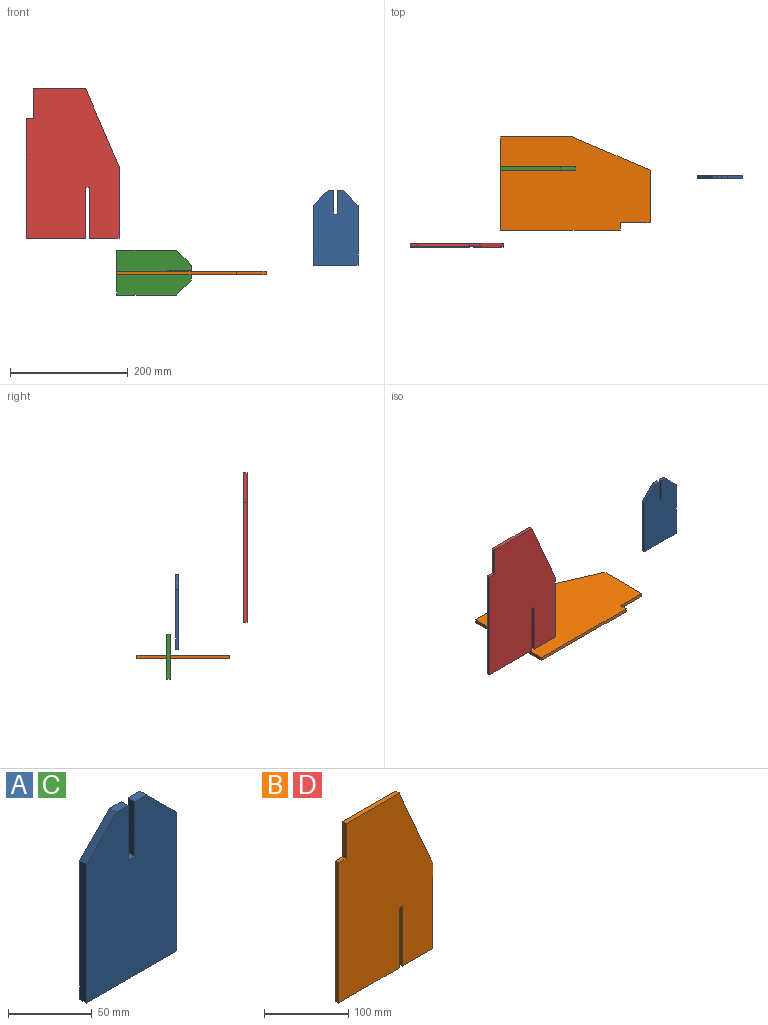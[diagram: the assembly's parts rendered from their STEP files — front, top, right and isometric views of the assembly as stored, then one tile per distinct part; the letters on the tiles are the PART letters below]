
ASSEMBLY  parts=4 mates=1
PART A: 12 faces, bbox 76.2x5.8x127 mm
  f0: plane 9.82x5.77mm, normal (0,0,1), area 56.6mm2, adj f1,f9,f10,f11
  f1: plane 25.4x25.4mm, normal (-0.71,0,0.71), area 207.1mm2, adj f0,f2,f10,f11
  f2: plane 101.6x5.77mm, normal (-1,0,0), area 585.8mm2, adj f1,f3,f10,f11
  f3: plane 76.2x5.77mm, normal (0,0,-1), area 439.4mm2, adj f2,f4,f10,f11
  f4: plane 101.6x5.77mm, normal (1,0,0), area 585.8mm2, adj f3,f5,f10,f11
  f5: plane 25.4x25.4mm, normal (0.71,0,0.71), area 207.1mm2, adj f4,f6,f10,f11
  f6: plane 9.82x5.77mm, normal (0,0,1), area 56.6mm2, adj f5,f7,f10,f11
  f7: plane 40.13x5.77mm, normal (-1,0,0), area 231.4mm2, adj f6,f8,f10,f11
  f8: plane 5.77x5.77mm, normal (0,0,1), area 33.2mm2, adj f7,f9,f10,f11
  f9: plane 40.13x5.77mm, normal (1,0,0), area 231.4mm2, adj f0,f8,f10,f11
  f10: plane 127x76.2mm, normal (0,-1,0), area 8800.8mm2, adj f0,f1,f2,f3,f4,f5,f6,f7
  f11: plane 127x76.2mm, normal (0,1,0), area 8800.8mm2, adj f0,f1,f2,f3,f4,f5,f6,f7
PART B: 13 faces, bbox 158.2x5.8x254 mm
  f0: plane 86.87x5.77mm, normal (1,0,0), area 500.9mm2, adj f1,f10,f11,f12
  f1: plane 5.77x5.77mm, normal (0,0,-1), area 33.2mm2, adj f0,f2,f11,f12
  f2: plane 86.86x5.77mm, normal (-1,0,0), area 500.8mm2, adj f1,f3,f11,f12
  f3: plane 50.8x5.77mm, normal (0,0,-1), area 292.9mm2, adj f2,f4,f11,f12
  f4: plane 122.77x5.77mm, normal (1,0,0), area 707.8mm2, adj f3,f5,f11,f12
  f5: plane 131.22x56.57mm, normal (0.92,0,0.4), area 823.9mm2, adj f4,f6,f11,f12
  f6: plane 88.9x5.77mm, normal (0,0,1), area 512.6mm2, adj f5,f7,f11,f12
  f7: plane 50.8x5.77mm, normal (-1,0,0), area 292.9mm2, adj f6,f8,f11,f12
  f8: plane 12.7x5.77mm, normal (0,0,1), area 73.2mm2, adj f7,f9,f11,f12
  f9: plane 203.2x5.77mm, normal (-1,0,0), area 1171.6mm2, adj f8,f10,f11,f12
  f10: plane 101.6x5.77mm, normal (0,0,-1), area 585.8mm2, adj f0,f9,f11,f12
  f11: plane 254x158.17mm, normal (0,-1,0), area 35316.1mm2, adj f0,f1,f2,f3,f4,f5,f6,f7
  f12: plane 254x158.17mm, normal (0,1,0), area 35316.1mm2, adj f0,f1,f2,f3,f4,f5,f6,f7
PART C: same geometry as A
PART D: same geometry as B
PLACE A t=(71.72,40.43,-17.32)mm
PLACE B rot(axis=(0.58,0.58,0.58),120deg) t=(-165,49.47,-90.5)mm
PLACE C rot(axis=(0.71,0,0.71),180deg) t=(-224.67,49.47,-105.73)mm
PLACE D t=(-340.36,-75.37,88.04)mm
MATE planar C.f11 <-> B.f0  axis (0,-1,0) through (-160.64,49.47,-90.15)mm
